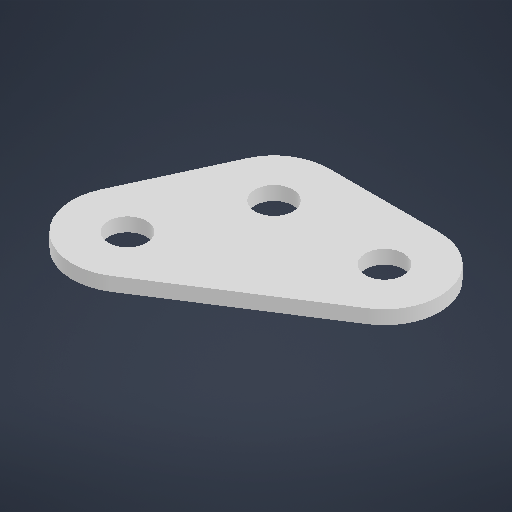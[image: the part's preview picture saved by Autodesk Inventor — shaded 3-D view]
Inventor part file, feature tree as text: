
AUTODESK INVENTOR PART (.ipt)
format: ipt  version: 2025.2 (Build 292293000, 293)  size: 186,368 bytes
history: native  units: in
note: dims shown in document units (in); Inventor stores cm internally (conversion verified against a paired STEP export)
features: extrude x1, sketch x1
ambient origin geometry x8: Origin, YZ Plane, XZ Plane, XY Plane, X Axis, Y Axis, Z Axis, Center Point
bodies: Solid1 (feature_tree)
feature tree (2):
  extrude  "Extrusion1"  Depth=0.0625in
  sketch  "Sketch1"  dims[d0=0.5in d1=0.5in d2=0.5in d3=0.0625in d4=0.0in]
